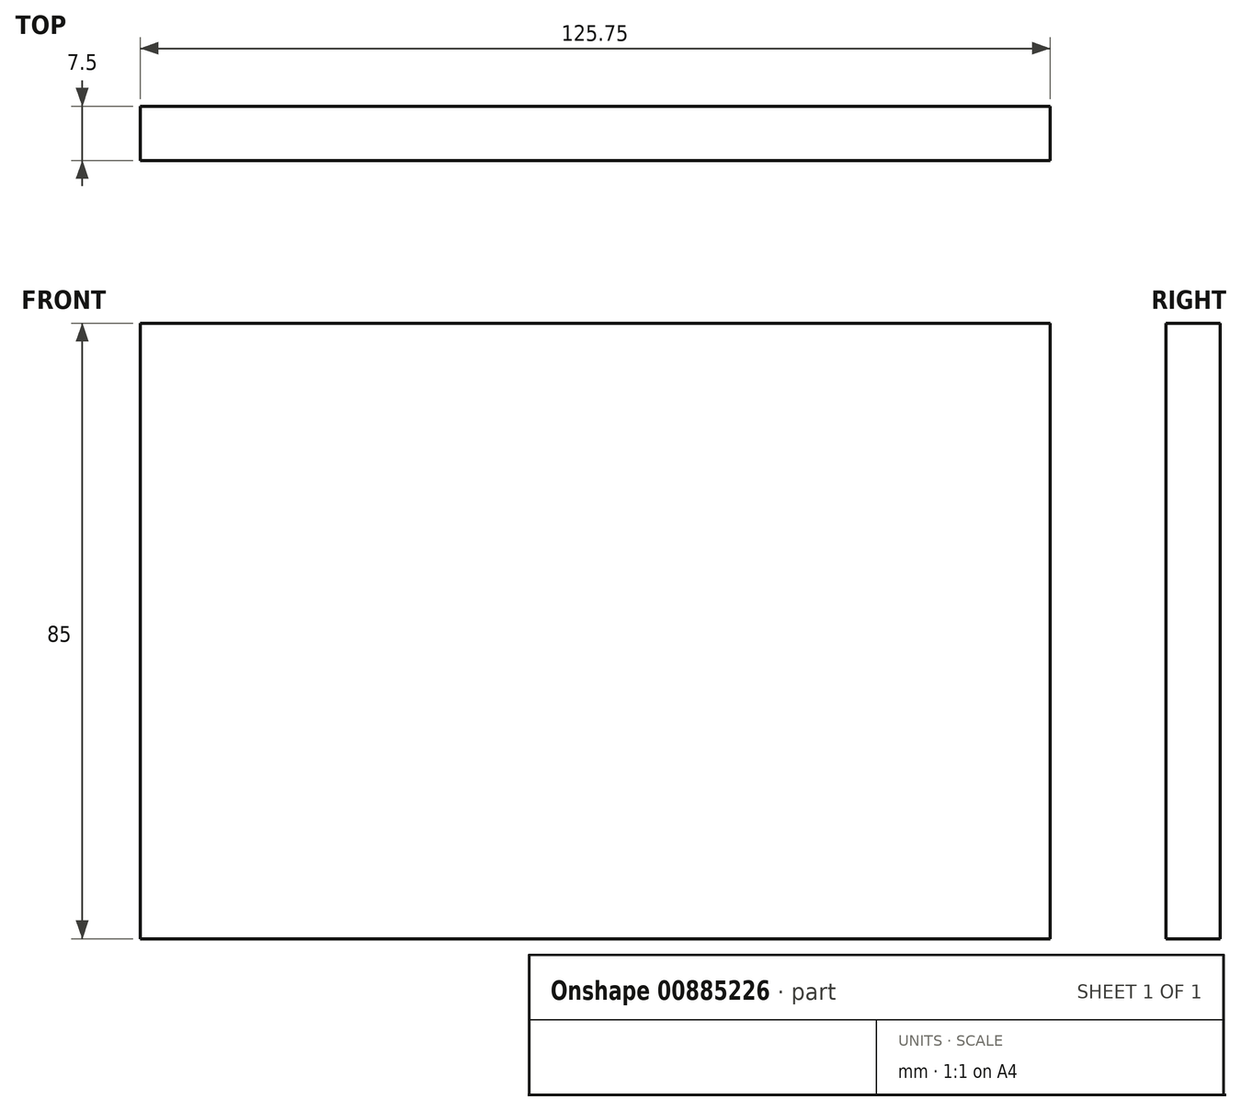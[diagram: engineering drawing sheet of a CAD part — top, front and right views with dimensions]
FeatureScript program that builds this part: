
annotation { "Feature Type Name" : "Feature", "Feature Type Description" : "" }
export const myFeature = defineFeature(function(context is Context, id is Id, definition is map)
    precondition{}
    {
        {
            var Q0;
            Q0=qCreatedBy(makeId("Front.planeOp"),FACE);
            var sketch = newSketch(context, id + "F0", { "sketchPlane" : qUnion([Q0])});
            skLineSegment(sketch, "E0.bottom", {"start": v(-85.19, 52.16) * mm, "end": v(40.56, 52.16) * mm});
            skLineSegment(sketch, "E0.top", {"start": v(-85.19, -32.84) * mm, "end": v(40.56, -32.84) * mm});
            skLineSegment(sketch, "E0.left", {"start": v(-85.19, 52.16) * mm, "end": v(-85.19, -32.84) * mm});
            skLineSegment(sketch, "E0.right", {"start": v(40.56, 52.16) * mm, "end": v(40.56, -32.84) * mm});
            skSolve(sketch);
        }
        {
            var Q0;
            Q0=makeQuery(id+"F0.imprint","IMPRINT",FACE,{"disambiguationData":[TD([[makeQuery(id+"F0.imprint","IMPRINT",EDGE,{"derivedFrom":sQuery(id+"F0.wireOp",EDGE,"E0.bottom")}),-1.0]])]});
            extrude(context, id + "F1", {"entities" : qUnion([Q0]), "depth" : 7.5 * mm, "offsetDistance" : 25 * mm});
        }
    });
